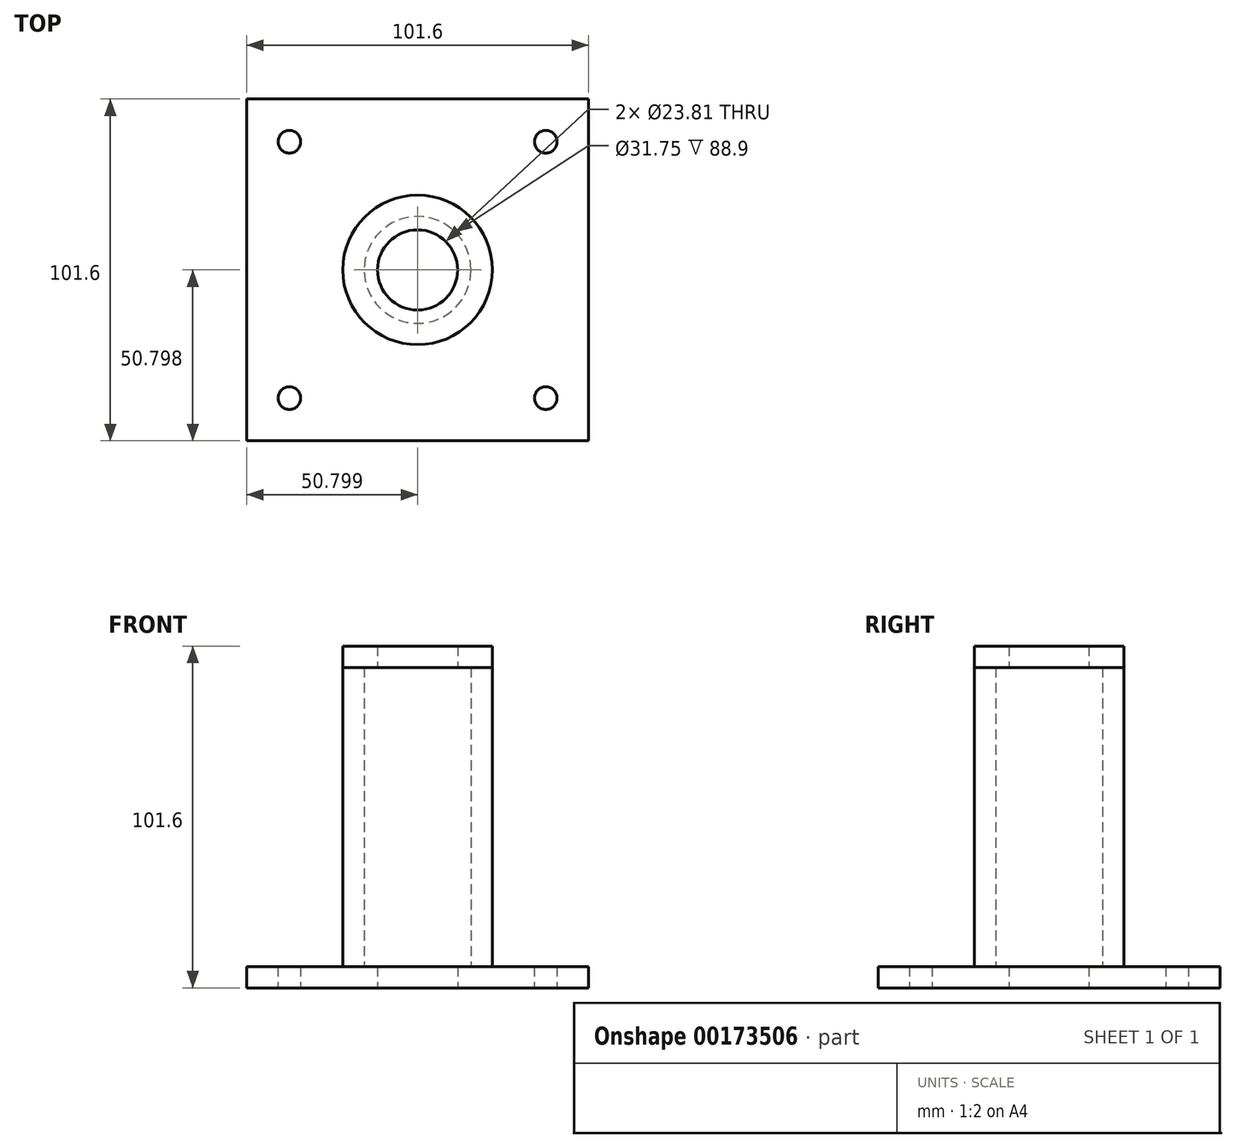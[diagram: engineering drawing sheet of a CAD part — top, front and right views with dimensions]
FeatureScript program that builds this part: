
annotation { "Feature Type Name" : "Feature", "Feature Type Description" : "" }
export const myFeature = defineFeature(function(context is Context, id is Id, definition is map)
    precondition{}
    {
        {
            var Q0;
            Q0=qCreatedBy(makeId("Top.planeOp"),FACE);
            var sketch = newSketch(context, id + "F0", { "sketchPlane" : qUnion([Q0])});
            skLineSegment(sketch, "E0.bottom", {"start": v(-48.54, 51.19) * mm, "end": v(53.06, 51.19) * mm});
            skLineSegment(sketch, "E0.top", {"start": v(-48.54, -50.41) * mm, "end": v(53.06, -50.41) * mm});
            skLineSegment(sketch, "E0.left", {"start": v(-48.54, 51.19) * mm, "end": v(-48.54, -50.41) * mm});
            skLineSegment(sketch, "E0.right", {"start": v(53.06, 51.19) * mm, "end": v(53.06, -50.41) * mm});
            skCircle(sketch, "E1", {"center": v(-35.84, 38.49) * mm, "radius": 3.37 * mm});
            skCircle(sketch, "E2", {"center": v(40.36, 38.49) * mm, "radius": 3.37 * mm});
            skCircle(sketch, "E3", {"center": v(-35.84, -37.71) * mm, "radius": 3.37 * mm});
            skCircle(sketch, "E4", {"center": v(40.36, -37.71) * mm, "radius": 3.37 * mm});
            skLineSegment(sketch, "E5", {"start": v(2.26, 51.19) * mm, "end": v(2.26, -50.41) * mm, "construction": true});
            skLineSegment(sketch, "E6.0", {"start": v(-48.54, 0.39) * mm, "end": v(53.06, 0.39) * mm, "construction": true});
            skCircle(sketch, "E7", {"center": v(2.26, 0.39) * mm, "radius": 11.9 * mm});
            skSolve(sketch);
        }
        {
            var Q0;
            Q0 = qSketchRegion(id + "F0", true);
            extrude(context, id + "F1", {"entities" : qUnion([Q0]), "depth" : 6.35 * mm});
        }
        {
            var Q0;
            Q0=makeQuery(id+"F1.opExtrude","CAP_FACE",FACE,{"disambiguationData":[OSD([sQuery(id+"F0.wireOp",EDGE,"E0.bottom"),sQuery(id+"F0.wireOp",EDGE,"E0.top"),sQuery(id+"F0.wireOp",EDGE,"E0.left"),sQuery(id+"F0.wireOp",EDGE,"E0.right"),sQuery(id+"F0.wireOp",EDGE,"E1"),sQuery(id+"F0.wireOp",EDGE,"E2"),sQuery(id+"F0.wireOp",EDGE,"E3"),sQuery(id+"F0.wireOp",EDGE,"E4"),sQuery(id+"F0.wireOp",EDGE,"E7")])],"isStart":false});
            var sketch = newSketch(context, id + "F2", { "sketchPlane" : qUnion([Q0])});
            skCircle(sketch, "E8.0", {"center": v(2.26, 0.39) * mm, "radius": 22.23 * mm});
            skCircle(sketch, "E9.0", {"center": v(2.26, 0.39) * mm, "radius": 15.87 * mm});
            skSolve(sketch);
        }
        {
            var Q0;
            Q0=makeQuery(id+"F2.imprint","IMPRINT",FACE,{"disambiguationData":[TD([[makeQuery(id+"F2.imprint","IMPRINT",EDGE,{"derivedFrom":sQuery(id+"F2.wireOp",EDGE,"E8.0")}),1.0]])]});
            extrude(context, id + "F3", {"entities" : qUnion([Q0]), "depth" : 88.9 * mm});
        }
        {
            var Q0;
            Q0=makeQuery(id+"F3.opExtrude","CAP_FACE",FACE,{"disambiguationData":[OSD([sQuery(id+"F2.wireOp",EDGE,"E8.0"),sQuery(id+"F2.wireOp",EDGE,"E9.0")])],"isStart":false});
            var sketch = newSketch(context, id + "F4", { "sketchPlane" : qUnion([Q0])});
            skCircle(sketch, "E10", {"center": v(2.26, 0.39) * mm, "radius": 22.23 * mm});
            skCircle(sketch, "E11", {"center": v(2.26, 0.39) * mm, "radius": 11.9 * mm});
            skSolve(sketch);
        }
        {
            var Q0;
            Q0 = qSketchRegion(id + "F4", true);
            extrude(context, id + "F5", {"entities" : qUnion([Q0]), "depth" : 6.35 * mm});
        }
    });
